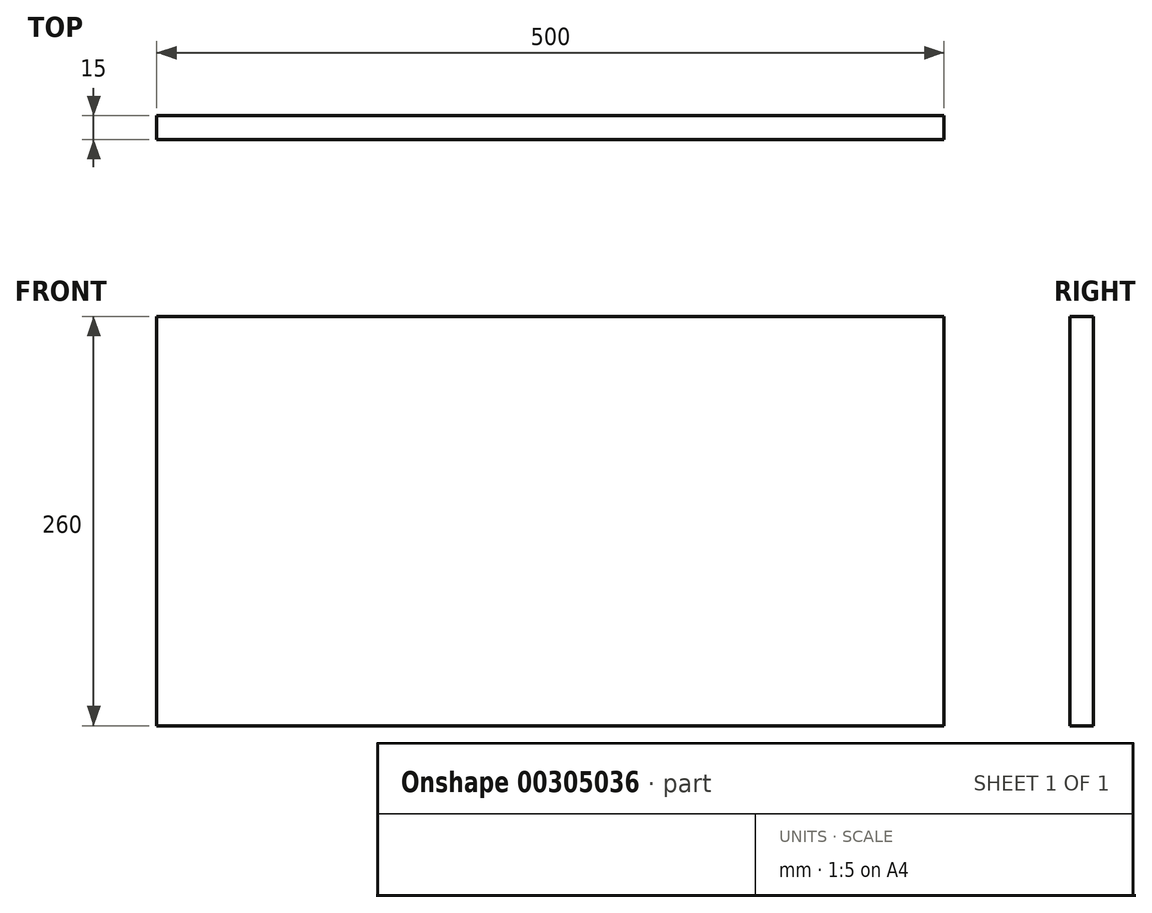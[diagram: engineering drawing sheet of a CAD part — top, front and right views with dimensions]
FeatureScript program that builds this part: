
annotation { "Feature Type Name" : "Feature", "Feature Type Description" : "" }
export const myFeature = defineFeature(function(context is Context, id is Id, definition is map)
    precondition{}
    {
        {
            var Q0;
            Q0=qCreatedBy(makeId("Front.planeOp"),FACE);
            var sketch = newSketch(context, id + "F0", { "sketchPlane" : qUnion([Q0])});
            skLineSegment(sketch, "E0.bottom", {"start": v(0, 0) * mm, "end": v(500, 0) * mm});
            skLineSegment(sketch, "E0.top", {"start": v(0, 260) * mm, "end": v(500, 260) * mm});
            skLineSegment(sketch, "E0.left", {"start": v(0, 0) * mm, "end": v(0, 260) * mm});
            skLineSegment(sketch, "E0.right", {"start": v(500, 0) * mm, "end": v(500, 260) * mm});
            skSolve(sketch);
        }
        {
            var Q0;
            Q0=makeQuery(id+"F0.imprint","IMPRINT",FACE,{"disambiguationData":[TD([[makeQuery(id+"F0.imprint","IMPRINT",EDGE,{"derivedFrom":sQuery(id+"F0.wireOp",EDGE,"E0.bottom")}),1.0]])]});
            extrude(context, id + "F1", {"entities" : qUnion([Q0]), "depth" : 15 * mm});
        }
    });
